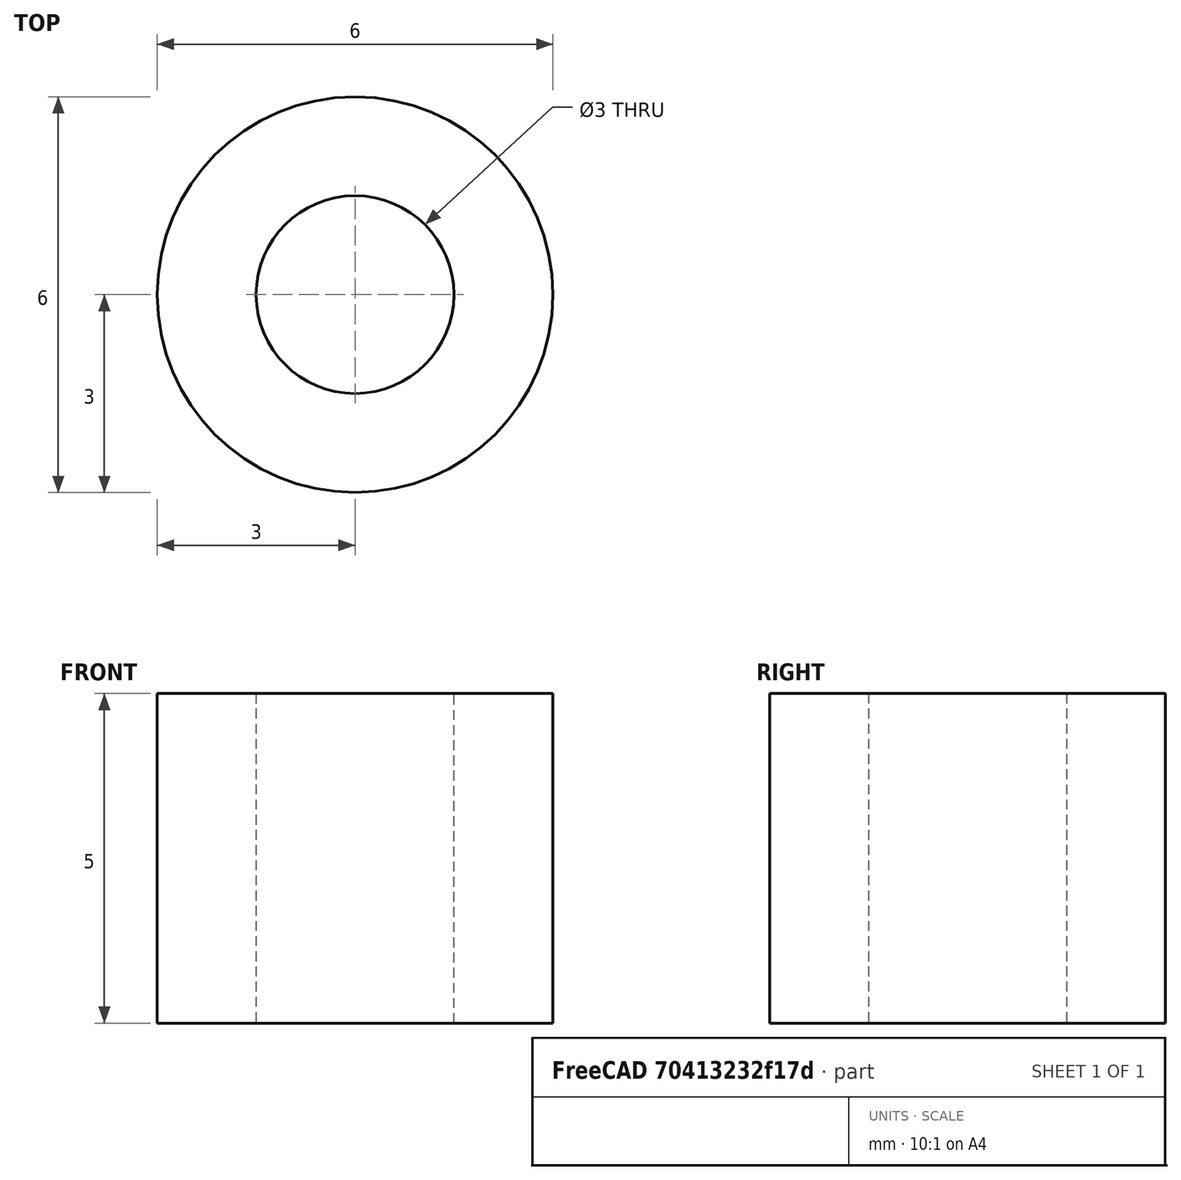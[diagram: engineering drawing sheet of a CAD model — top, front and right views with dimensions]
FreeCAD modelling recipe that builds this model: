
FCSTD DOCUMENT  (FreeCAD 0.18R16131 (Git))
Label: entetoise
License: All rights reserved
LicenseURL: http://en.wikipedia.org/wiki/All_rights_reserved
objects: Sketcher::SketchObject×1, PartDesign::Pad×1, PartDesign::Body×1
note: 4 computed .brp shape members not serialized (recipe doc carries the construction recipe); baked Part::Feature solids carry a one-line shape summary decoded from their .brp

FEATURE [Sketcher::SketchObject] Sketch
  MapMode = 5
  Support = -> [XY_Plane]
  sketch-geometry (2):
    g0: Circle CenterX=0 CenterY=0 CenterZ=0 NormalX=0 NormalY=0 NormalZ=1 AngleXU=0 Radius=1.5
    g1: Circle CenterX=0 CenterY=0 CenterZ=0 NormalX=0 NormalY=0 NormalZ=1 AngleXU=0 Radius=3
  constraints (4):
    c: Coincident(g0,g-1)
    c: Diameter(g0) = 3
    c: Coincident(g1,g0)
    c: Diameter(g1) = 6
FEATURE [PartDesign::Pad] Pad
  Length = 5
  Length2 = 100
  Profile = -> Sketch
  Type = 0
FEATURE [PartDesign::Body] Body
  Group = -> [Sketch,Pad]
  Origin = -> Origin
  Tip = -> Pad
